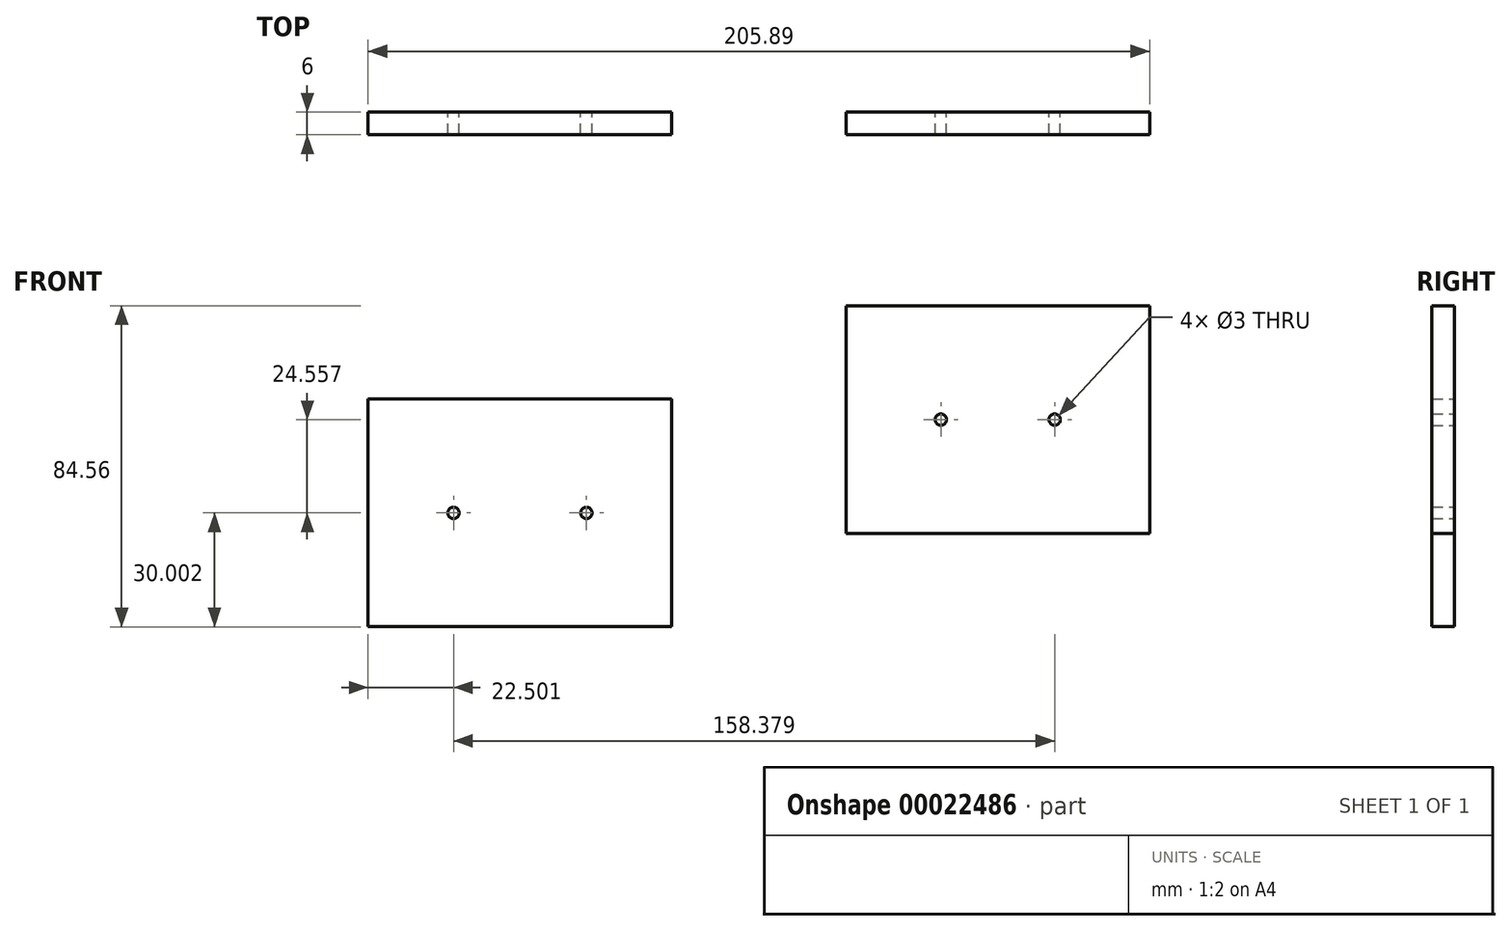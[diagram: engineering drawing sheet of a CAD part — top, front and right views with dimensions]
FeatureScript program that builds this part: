
annotation { "Feature Type Name" : "Feature", "Feature Type Description" : "" }
export const myFeature = defineFeature(function(context is Context, id is Id, definition is map)
    precondition{}
    {
        {
            var Q0;
            Q0=qCreatedBy(makeId("Front.planeOp"),FACE);
            var sketch = newSketch(context, id + "F0", { "sketchPlane" : qUnion([Q0])});
            skLineSegment(sketch, "E0.bottom", {"start": v(-42.38, 40.37) * mm, "end": v(37.62, 40.37) * mm});
            skLineSegment(sketch, "E0.top", {"start": v(-42.38, -19.63) * mm, "end": v(37.62, -19.63) * mm});
            skLineSegment(sketch, "E0.left", {"start": v(-42.38, 40.37) * mm, "end": v(-42.38, -19.63) * mm});
            skLineSegment(sketch, "E0.right", {"start": v(37.62, 40.37) * mm, "end": v(37.62, -19.63) * mm});
            skLineSegment(sketch, "E1", {"start": v(-42.38, 10.37) * mm, "end": v(37.62, 10.37) * mm});
            skPoint(sketch, "E2", {"position": v(-17.38, 10.37) * mm});
            skPoint(sketch, "E3", {"position": v(12.6, 10.37) * mm});
            skCircle(sketch, "E4", {"center": v(-17.38, 10.37) * mm, "radius": 1.5 * mm});
            skCircle(sketch, "E5", {"center": v(12.6, 10.37) * mm, "radius": 1.5 * mm});
            skSolve(sketch);
        }
        {
            var Q0;
            Q0=makeQuery(id+"F0.imprint","IMPRINT",FACE,{"disambiguationData":[TD([[makeQuery(id+"F0.imprint","IMPRINT",EDGE,{"derivedFrom":sQuery(id+"F0.wireOp",EDGE,"E0.bottom")}),-1.0]])]});
            var Q1;
            {var subQ2=sQuery(id+"F0.wireOp",EDGE,"E0.top");Q1=makeQuery(id+"F0.imprint","IMPRINT",FACE,{"disambiguationData":[TD([[makeQuery(id+"F0.imprint","IMPRINT",EDGE,{"derivedFrom":subQ2}),1.0]])]});}
            extrude(context, id + "F1", {"entities" : qUnion([Q0, Q1]), "depth" : 6 * mm});
        }
        {
            var Q0;
            Q0=qCreatedBy(makeId("Front.planeOp"),FACE);
            var sketch = newSketch(context, id + "F2", { "sketchPlane" : qUnion([Q0])});
            skLineSegment(sketch, "E6.bottom", {"start": v(-168.27, 15.8) * mm, "end": v(-88.27, 15.8) * mm});
            skLineSegment(sketch, "E6.top", {"start": v(-168.27, -44.19) * mm, "end": v(-88.27, -44.19) * mm});
            skLineSegment(sketch, "E6.left", {"start": v(-168.27, 15.8) * mm, "end": v(-168.27, -44.19) * mm});
            skLineSegment(sketch, "E6.right", {"start": v(-88.27, 15.8) * mm, "end": v(-88.27, -44.19) * mm});
            skLineSegment(sketch, "E7", {"start": v(-168.27, -14.19) * mm, "end": v(-88.27, -14.19) * mm});
            skLineSegment(sketch, "E8", {"start": v(-88.27, -14.19) * mm, "end": v(-110.77, -14.19) * mm});
            skLineSegment(sketch, "E9", {"start": v(-168.27, -14.19) * mm, "end": v(-145.77, -14.19) * mm});
            skCircle(sketch, "E10", {"center": v(-145.77, -14.19) * mm, "radius": 1.5 * mm});
            skCircle(sketch, "E11", {"center": v(-110.77, -14.19) * mm, "radius": 1.5 * mm});
            skSolve(sketch);
        }
        {
            var Q0;
            {var subQ13=sQuery(id+"F2.wireOp",EDGE,"E6.bottom");Q0=makeQuery(id+"F2.imprint","IMPRINT",FACE,{"disambiguationData":[TD([[makeQuery(id+"F2.imprint","IMPRINT",EDGE,{"derivedFrom":subQ13}),-1.0]])]});}
            var Q1;
            {var subQ13=sQuery(id+"F2.wireOp",EDGE,"E6.top");Q1=makeQuery(id+"F2.imprint","IMPRINT",FACE,{"disambiguationData":[TD([[makeQuery(id+"F2.imprint","IMPRINT",EDGE,{"derivedFrom":subQ13}),1.0]])]});}
            extrude(context, id + "F3", {"entities" : qUnion([Q0, Q1]), "depth" : 6 * mm});
        }
    });
